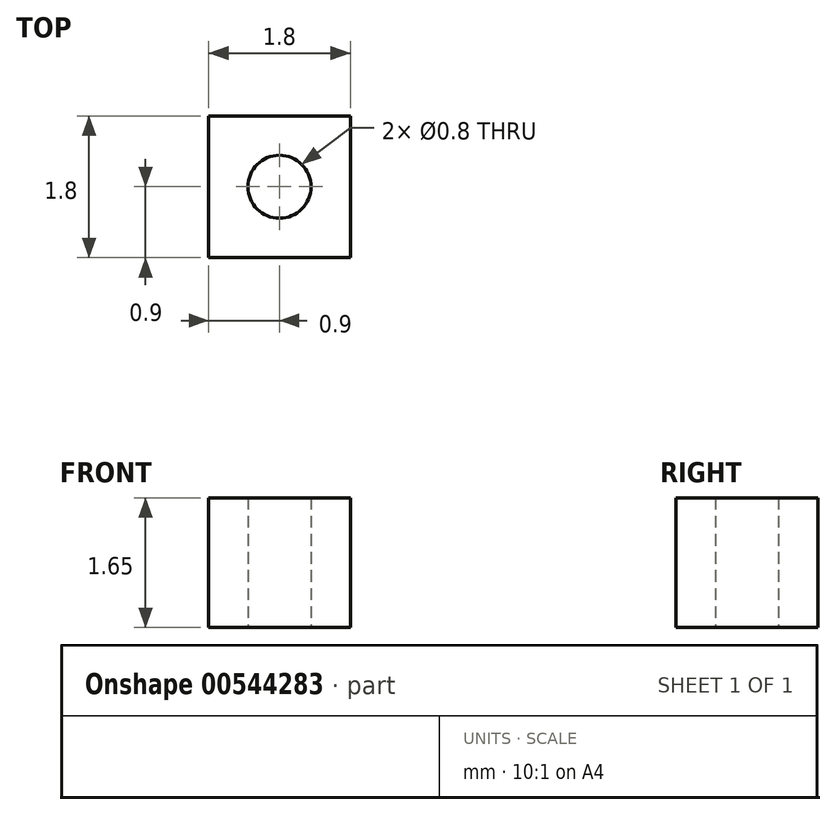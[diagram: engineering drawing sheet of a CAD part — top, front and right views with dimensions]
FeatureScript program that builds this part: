
annotation { "Feature Type Name" : "Feature", "Feature Type Description" : "" }
export const myFeature = defineFeature(function(context is Context, id is Id, definition is map)
    precondition{}
    {
        {
            var Q0;
            Q0=qCreatedBy(makeId("Top.planeOp"),FACE);
            var sketch = newSketch(context, id + "F0", { "sketchPlane" : qUnion([Q0])});
            skLineSegment(sketch, "E0.bottom", {"start": v(0, 0) * mm, "end": v(1.8, 0) * mm});
            skLineSegment(sketch, "E0.top", {"start": v(0, 1.8) * mm, "end": v(1.8, 1.8) * mm});
            skLineSegment(sketch, "E0.left", {"start": v(0, 0) * mm, "end": v(0, 1.8) * mm});
            skLineSegment(sketch, "E0.right", {"start": v(1.8, 0) * mm, "end": v(1.8, 1.8) * mm});
            skCircle(sketch, "E1", {"center": v(0.9, 0.9) * mm, "radius": 0.4 * mm});
            skSolve(sketch);
        }
        {
            var Q0;
            Q0=qSketchRegion(id+"F0",true);
            extrude(context, id + "F1", {"entities" : qUnion([Q0]), "depth" : 1.65 * mm});
        }
    });
